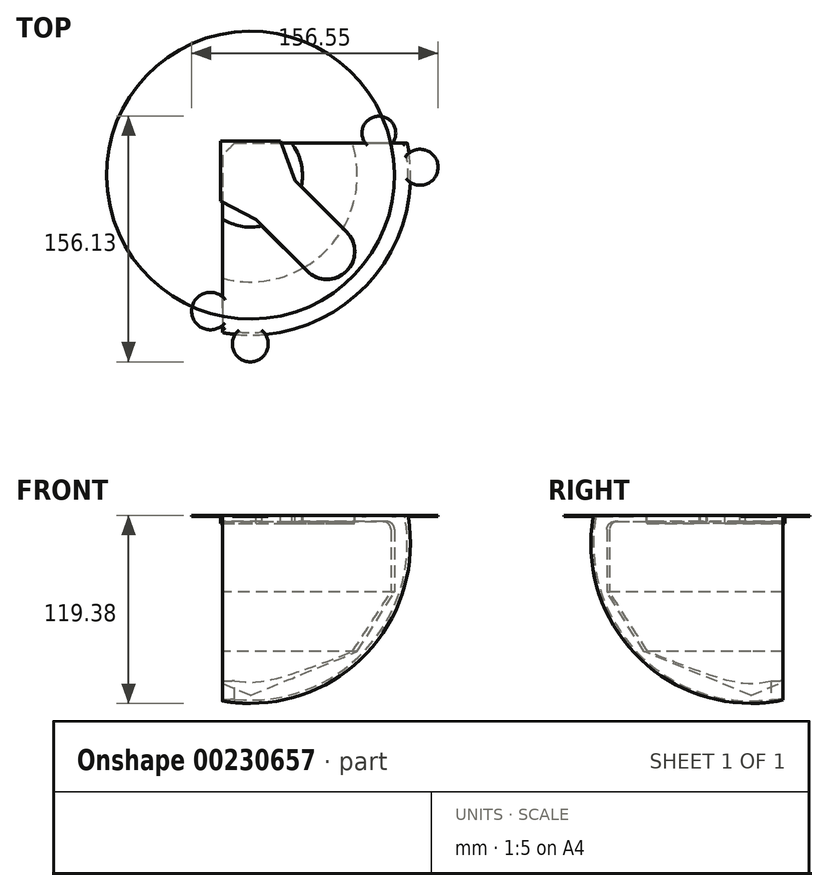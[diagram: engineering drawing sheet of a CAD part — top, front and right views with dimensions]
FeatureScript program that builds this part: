
annotation { "Feature Type Name" : "Feature", "Feature Type Description" : "" }
export const myFeature = defineFeature(function(context is Context, id is Id, definition is map)
    precondition{}
    {
        {
            var Q0;
            Q0=qCreatedBy(makeId("Front.planeOp"),FACE);
            var sketch = newSketch(context, id + "F0", { "sketchPlane" : qUnion([Q0])});
            skArc(sketch, "E0", {"start": v(17.78, 101.6) * mm, "mid": v(119.38, 0) * mm, "end": v(17.78, -101.6) * mm});
            skLineSegment(sketch, "E1", {"start": v(17.78, 101.6) * mm, "end": v(17.78, -101.6) * mm});
            skLineSegment(sketch, "E2", {"start": v(0, 0) * mm, "end": v(0, -88.7) * mm, "construction": true});
            skLineSegment(sketch, "E3", {"start": v(0, 17.78) * mm, "end": v(166.86, 17.78) * mm, "construction": true});
            skSolve(sketch);
        }
        {
            var Q0;
            Q0 = qSketchRegion(id + "F0", true);
            var Q1;
            Q1=sQuery(id+"F0.wireOp",EDGE,"E1");
            revolve(context, id + "F1", {"entities" : qUnion([Q0]), "axis" : qUnion([Q1]), "revolveType" : RevolveType.FULL});
        }
        {
            var Q0;
            Q0=qCreatedBy(makeId("Front.planeOp"),FACE);
            var sketch = newSketch(context, id + "F2", { "sketchPlane" : qUnion([Q0])});
            skLineSegment(sketch, "E4.0", {"start": v(0, 17.78) * mm, "end": v(166.86, 17.78) * mm});
            skLineSegment(sketch, "E5.0", {"start": v(0, 17.78) * mm, "end": v(0, -149.14) * mm});
            skArc(sketch, "E6", {"start": v(166.86, 17.78) * mm, "mid": v(-88.49, 106.18) * mm, "end": v(0, -149.14) * mm});
            skPoint(sketch, "E7.orphan", {"position": v(0, -88.7) * mm});
            skPoint(sketch, "E8.orphan", {"position": v(0, 0) * mm});
            skSolve(sketch);
        }
        {
            var Q0;
            Q0 = qSketchRegion(id + "F2", true);
            extrude(context, id + "F3", {"entities" : qUnion([Q0]), "operationType" : NewBodyOperationType.REMOVE, "endBound" : BoundingType.SYMMETRIC, "oppositeDirection" : true, "depth" : 254 * mm});
        }
        {
            var Q0;
            Q0=qCreatedBy(makeId("Right.planeOp"),FACE);
            var sketch = newSketch(context, id + "F4", { "sketchPlane" : qUnion([Q0])});
            skLineSegment(sketch, "E9.bottom", {"start": v(20.32, 38.1) * mm, "end": v(156.34, 38.1) * mm});
            skLineSegment(sketch, "E9.top", {"start": v(20.32, -154.57) * mm, "end": v(156.34, -154.57) * mm});
            skLineSegment(sketch, "E9.left", {"start": v(20.32, 38.1) * mm, "end": v(20.32, -154.57) * mm});
            skLineSegment(sketch, "E9.right", {"start": v(156.34, 38.1) * mm, "end": v(156.34, -154.57) * mm});
            skLineSegment(sketch, "E10.0", {"start": v(-100.03, 17.78) * mm, "end": v(100.03, 17.78) * mm});
            skSolve(sketch);
        }
        {
            var Q0;
            Q0 = qSketchRegion(id + "F4", true);
            extrude(context, id + "F5", {"entities" : qUnion([Q0]), "operationType" : NewBodyOperationType.REMOVE, "endBound" : BoundingType.SYMMETRIC, "oppositeDirection" : true, "depth" : 508 * mm});
        }
        {
            var Q0;
            Q0=qCreatedBy(makeId("Front.planeOp"),FACE);
            var sketch = newSketch(context, id + "F6", { "sketchPlane" : qUnion([Q0])});
            skLineSegment(sketch, "E11.0", {"start": v(17.78, 101.6) * mm, "end": v(17.78, -101.6) * mm});
            skLineSegment(sketch, "E12", {"start": v(17.78, -96.52) * mm, "end": v(85.58, -68.7) * mm});
            skLineSegment(sketch, "E13", {"start": v(85.58, -68.7) * mm, "end": v(109.22, -30.9) * mm});
            skLineSegment(sketch, "E14", {"start": v(109.22, -30.9) * mm, "end": v(109.22, 13.97) * mm});
            skLineSegment(sketch, "E15", {"start": v(109.22, 13.97) * mm, "end": v(50.8, 13.97) * mm});
            skLineSegment(sketch, "E16", {"start": v(50.8, 13.97) * mm, "end": v(50.8, 17.78) * mm});
            skLineSegment(sketch, "E17", {"start": v(50.8, 17.78) * mm, "end": v(17.78, 17.78) * mm});
            skLineSegment(sketch, "E18.0", {"start": v(0, 17.78) * mm, "end": v(166.86, 17.78) * mm});
            skCircle(sketch, "E19", {"center": v(17.78, 0) * mm, "radius": 96.52 * mm, "construction": true});
            skArc(sketch, "E20.0", {"start": v(17.78, 101.6) * mm, "mid": v(119.38, 0) * mm, "end": v(17.78, -101.6) * mm, "construction": true});
            skSolve(sketch);
        }
        {
            var Q0;
            Q0 = qSketchRegion(id + "F6", true);
            var Q1;
            Q1=sQuery(id+"F6.wireOp",EDGE,"E11.0");
            revolve(context, id + "F7", {"operationType" : NewBodyOperationType.REMOVE, "entities" : qUnion([Q0]), "axis" : qUnion([Q1]), "revolveType" : RevolveType.FULL, "oppositeDirection" : true});
        }
        {
            var Q0;
            Q0=makeQuery(id+"F7D0zQtabOIinPC_1.boolean.opBoolean","MERGE",EDGE,{"derivedFrom":[makeQuery(id+"F5.boolean.opBoolean","INTERSECT",EDGE,{"derivedFrom":[makeQuery(id+"F3.boolean.opBoolean","COPY",FACE,{"derivedFrom":makeQuery(id+"F3.opExtrude","SWEPT_FACE",FACE,{"disambiguationData":[OSD([sQuery(id+"F2.wireOp",EDGE,"E5.0")])]})}),makeQuery(id+"F5.opExtrude","SWEPT_FACE",FACE,{"disambiguationData":[OSD([sQuery(id+"F4.wireOp",EDGE,"E9.left")])]})]}),makeQuery(id+"F7D0zQtabOIinPC_1.opExtrude","CAP_EDGE",EDGE,{"disambiguationData":[OSD([sQuery(id+"FqHA2hHfJR45taR_1.wireOp",EDGE,"DHEgjYGF-QrFT-lqQP-OPns-Nrnl5IJyqBDY")])],"isStart":true})]});
            chamfer(context, id + "F8", {"entities" : qUnion([Q0]), "width" : 7.62 * mm, "tangentPropagation" : true});
        }
        {
            var Q0;
            Q0=makeQuery(id+"F7.boolean.opBoolean","SPLIT",FACE,{"disambiguationData":[TD([makeQuery(id+"F1.opRevolve","SWEPT_FACE",FACE,{"disambiguationData":[OSD([sQuery(id+"F0.wireOp",EDGE,"E0")])]}),makeQuery(id+"F3.boolean.opBoolean","COPY",FACE,{"derivedFrom":makeQuery(id+"F3.opExtrude","SWEPT_FACE",FACE,{"disambiguationData":[OSD([sQuery(id+"F2.wireOp",EDGE,"E5.0")])]})}),makeQuery(id+"F5.boolean.opBoolean","COPY",FACE,{"derivedFrom":makeQuery(id+"F5.opExtrude","SWEPT_FACE",FACE,{"disambiguationData":[OSD([sQuery(id+"F4.wireOp",EDGE,"E9.left")])]})}),makeQuery(id+"F7.opRevolve","SWEPT_FACE",FACE,{"disambiguationData":[OSD([sQuery(id+"F6.wireOp",EDGE,"E16")])]})])],"derivedFrom":makeQuery(id+"F3.boolean.opBoolean","COPY",FACE,{"derivedFrom":makeQuery(id+"F3.opExtrude","SWEPT_FACE",FACE,{"disambiguationData":[OSD([sQuery(id+"F2.wireOp",EDGE,"E4.0")])]})})});
            var sketch = newSketch(context, id + "F9", { "sketchPlane" : qUnion([Q0])});
            skLineSegment(sketch, "E21", {"start": v(17.78, 0) * mm, "end": v(66.27, -48.5) * mm, "construction": true});
            skArc(sketch, "E22.0.startCap", {"start": v(5.2, -12.57) * mm, "mid": v(5.2, 12.57) * mm, "end": v(30.35, 12.57) * mm});
            skArc(sketch, "E22.0.endCap", {"start": v(78.85, -35.92) * mm, "mid": v(78.85, -61.07) * mm, "end": v(53.7, -61.07) * mm});
            skLineSegment(sketch, "E22.0.left", {"start": v(30.35, 12.57) * mm, "end": v(78.85, -35.92) * mm});
            skLineSegment(sketch, "E22.0.right", {"start": v(5.2, -12.57) * mm, "end": v(53.7, -61.07) * mm});
            skSolve(sketch);
        }
        {
            var Q0;
            Q0 = qSketchRegion(id + "F9", true);
            extrude(context, id + "F10", {"entities" : qUnion([Q0]), "operationType" : NewBodyOperationType.REMOVE, "oppositeDirection" : true, "depth" : 10.16 * mm});
        }
        {
            var Q0;
            Q0=makeQuery(id+"F7.boolean.opBoolean","COPY",EDGE,{"derivedFrom":makeQuery(id+"F7.opRevolve","SWEPT_EDGE",EDGE,{"disambiguationData":[OSD([sQuery(id+"F6.wireOp",EDGE,"E14"),sQuery(id+"F6.wireOp",EDGE,"E15")])]})});
            fillet(context, id + "F11", {"entities" : qUnion([Q0]), "radius" : 5.08 * mm, "tangentPropagation" : true, "allowEdgeOverflow" : false});
        }
        {
            var Q0;
            Q0=makeQuery(id+"F3.boolean.opBoolean","COPY",EDGE,{"derivedFrom":makeQuery(id+"F3.opExtrude","SWEPT_EDGE",EDGE,{"disambiguationData":[OSD([sQuery(id+"F2.wireOp",EDGE,"E4.0"),sQuery(id+"F2.wireOp",EDGE,"E5.0")])]})});
            var Q1;
            Q1=makeQuery(id+"F5.boolean.opBoolean","INTERSECT",EDGE,{"derivedFrom":[makeQuery(id+"F3.boolean.opBoolean","COPY",FACE,{"derivedFrom":makeQuery(id+"F3.opExtrude","SWEPT_FACE",FACE,{"disambiguationData":[OSD([sQuery(id+"F2.wireOp",EDGE,"E4.0")])]})}),makeQuery(id+"F5.opExtrude","SWEPT_FACE",FACE,{"disambiguationData":[OSD([sQuery(id+"F4.wireOp",EDGE,"E9.left")])]})]});
            var Q2;
            Q2=makeQuery(id+"F3.boolean.opBoolean","INTERSECT",EDGE,{"derivedFrom":[makeQuery(id+"F1.opRevolve","SWEPT_FACE",FACE,{"disambiguationData":[OSD([sQuery(id+"F0.wireOp",EDGE,"E0")])]}),makeQuery(id+"F3.opExtrude","SWEPT_FACE",FACE,{"disambiguationData":[OSD([sQuery(id+"F2.wireOp",EDGE,"E4.0")])]})]});
            fillet(context, id + "F12", {"entities" : qUnion([Q0, Q1, Q2]), "radius" : 1.52 * mm, "tangentPropagation" : true, "allowEdgeOverflow" : false});
        }
        {
            var Q0;
            Q0=makeQuery(id+"F3.boolean.opBoolean","COPY",FACE,{"derivedFrom":makeQuery(id+"F3.opExtrude","SWEPT_FACE",FACE,{"disambiguationData":[OSD([sQuery(id+"F2.wireOp",EDGE,"E4.0")])]})});
            var sketch = newSketch(context, id + "F13", { "sketchPlane" : qUnion([Q0])});
            skLineSegment(sketch, "E23", {"start": v(17.78, 0) * mm, "end": v(66.27, -48.5) * mm, "construction": true});
            skArc(sketch, "E24.0.startCap", {"start": v(5.39, -12.4) * mm, "mid": v(5.39, 12.4) * mm, "end": v(30.17, 12.4) * mm});
            skArc(sketch, "E24.0.endCap", {"start": v(78.67, -36.1) * mm, "mid": v(78.67, -60.89) * mm, "end": v(53.88, -60.89) * mm});
            skLineSegment(sketch, "E24.0.left", {"start": v(30.17, 12.4) * mm, "end": v(78.67, -36.1) * mm});
            skLineSegment(sketch, "E24.0.right", {"start": v(5.39, -12.4) * mm, "end": v(53.88, -60.89) * mm});
            skLineSegment(sketch, "E25", {"start": v(-1.27, -16.5) * mm, "end": v(-1.27, 21.6) * mm});
            skLineSegment(sketch, "E26", {"start": v(-1.27, 21.6) * mm, "end": v(36.83, 21.6) * mm});
            skLineSegment(sketch, "E27", {"start": v(36.83, 21.6) * mm, "end": v(45.9, -3.34) * mm});
            skLineSegment(sketch, "E28", {"start": v(-1.27, -16.5) * mm, "end": v(21.25, -28.26) * mm});
            skFitSpline(sketch, "E29.0", {"points": [v(7.62, 20.32) * mm, v(34.63, 20.32) * mm, v(61.63, 20.32) * mm, v(88.64, 20.32) * mm], "construction": true});
            skSolve(sketch);
        }
        {
            var Q0;
            Q0 = qSketchRegion(id + "F13", true);
            extrude(context, id + "F14", {"entities" : qUnion([Q0]), "oppositeDirection" : true, "depth" : 5.08 * mm});
        }
        {
            var Q0;
            Q0=makeQuery(id+"F3.boolean.opBoolean","COPY",FACE,{"derivedFrom":makeQuery(id+"F3.opExtrude","SWEPT_FACE",FACE,{"disambiguationData":[OSD([sQuery(id+"F2.wireOp",EDGE,"E4.0")])]})});
            var sketch = newSketch(context, id + "F15", { "sketchPlane" : qUnion([Q0])});
            skCircle(sketch, "E30", {"center": v(125.5, 5.02) * mm, "radius": 11.42 * mm});
            skCircle(sketch, "E31", {"center": v(99.33, 26.76) * mm, "radius": 10.72 * mm});
            skCircle(sketch, "E32", {"center": v(17.62, -107.28) * mm, "radius": 11.37 * mm});
            skCircle(sketch, "E33", {"center": v(-7.73, -86.35) * mm, "radius": 11.91 * mm});
            skSolve(sketch);
        }
        {
            var Q0;
            Q0 = qSketchRegion(id + "F15", true);
            extrude(context, id + "F16", {"entities" : qUnion([Q0]), "operationType" : NewBodyOperationType.ADD, "oppositeDirection" : true, "depth" : 0.64 * mm});
        }
    });
